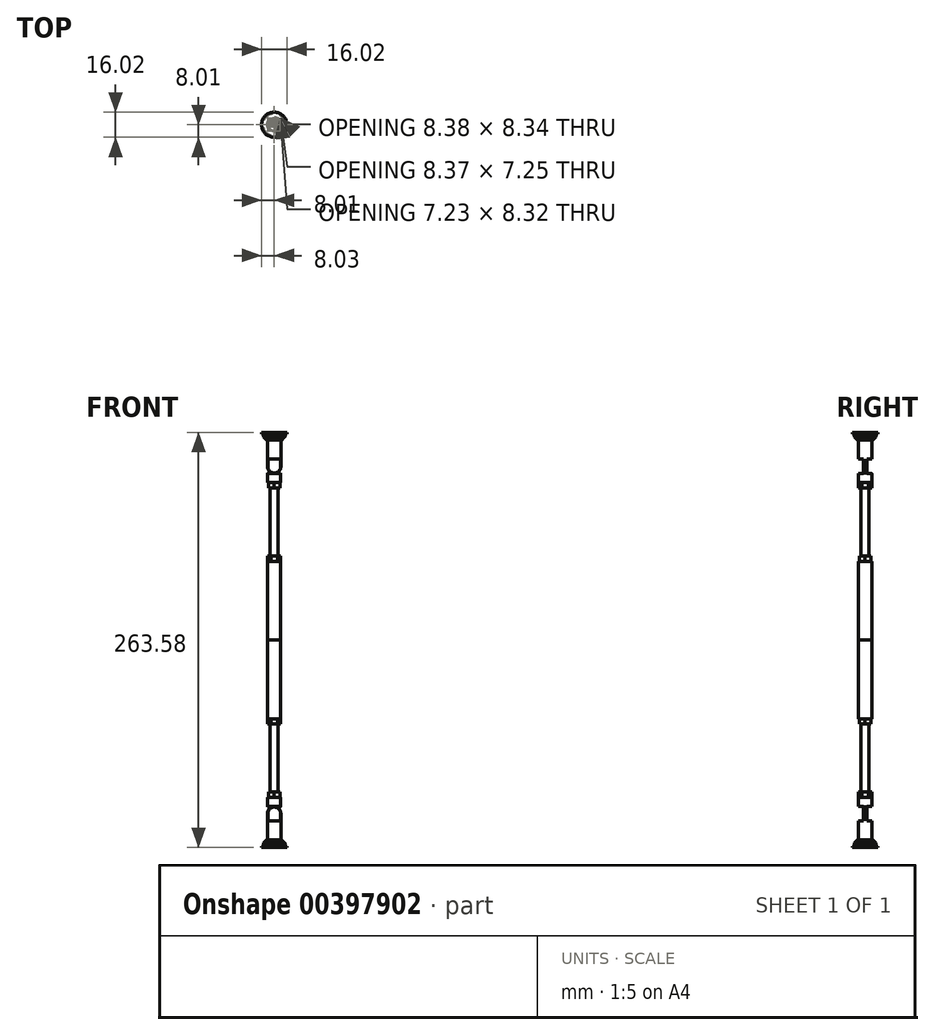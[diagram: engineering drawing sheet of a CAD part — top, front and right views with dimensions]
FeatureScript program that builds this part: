
annotation { "Feature Type Name" : "Feature", "Feature Type Description" : "" }
export const myFeature = defineFeature(function(context is Context, id is Id, definition is map)
    precondition{}
    {
        {
            var Q0;
            Q0=qCreatedBy(makeId("Top.planeOp"),FACE);
            var sketch = newSketch(context, id + "F0", { "sketchPlane" : qUnion([Q0])});
            skCircle(sketch, "E0", {"center": v(0, 0) * mm, "radius": 4.2 * mm});
            skSolve(sketch);
        }
        {
            var Q0;
            Q0 = qSketchRegion(id + "F0", true);
            extrude(context, id + "F1", {"entities" : qUnion([Q0]), "depth" : 50 * mm});
        }
        {
            var Q0;
            Q0=qCreatedBy(makeId("Top.planeOp"),FACE);
            var sketch = newSketch(context, id + "F2", { "sketchPlane" : qUnion([Q0])});
            skCircle(sketch, "E1", {"center": v(0, 0) * mm, "radius": 2.52 * mm});
            skSolve(sketch);
        }
        {
            var Q0;
            Q0 = qSketchRegion(id + "F2", true);
            extrude(context, id + "F3", {"entities" : qUnion([Q0]), "depth" : 100 * mm});
        }
        {
            var Q0;
            Q0=makeQuery(id+"F1.opExtrude","CAP_FACE",FACE,{"disambiguationData":[OSD([sQuery(id+"F0.wireOp",EDGE,"E0")])],"isStart":false});
            var sketch = newSketch(context, id + "F4", { "sketchPlane" : qUnion([Q0])});
            skCircle(sketch, "E2.cCircle", {"center": v(0, 0) * mm, "radius": 3.62 * mm, "construction": true});
            skLineSegment(sketch, "E2.0", {"start": v(-2.1, 3.62) * mm, "end": v(2.1, 3.62) * mm});
            skLineSegment(sketch, "E2.1", {"start": v(2.1, 3.62) * mm, "end": v(4.18, 0) * mm});
            skLineSegment(sketch, "E2.2", {"start": v(4.18, 0) * mm, "end": v(2.1, -3.62) * mm});
            skLineSegment(sketch, "E2.3", {"start": v(2.1, -3.62) * mm, "end": v(-2.1, -3.62) * mm});
            skLineSegment(sketch, "E2.4", {"start": v(-2.1, -3.62) * mm, "end": v(-4.18, 0) * mm});
            skLineSegment(sketch, "E2.5", {"start": v(-4.18, 0) * mm, "end": v(-2.1, 3.62) * mm});
            skPoint(sketch, "E2.0.midPoint", {"position": v(0, 3.62) * mm});
            skSolve(sketch);
        }
        {
            var Q0;
            Q0 = qSketchRegion(id + "F4", true);
            extrude(context, id + "F5", {"entities" : qUnion([Q0]), "operationType" : NewBodyOperationType.ADD, "depth" : 3.4 * mm});
        }
        {
            var Q0;
            Q0=makeQuery(id+"F3.opExtrude","CAP_FACE",FACE,{"disambiguationData":[OSD([sQuery(id+"F2.wireOp",EDGE,"E1")])],"isStart":false});
            var sketch = newSketch(context, id + "F6", { "sketchPlane" : qUnion([Q0])});
            skCircle(sketch, "E3.cCircle", {"center": v(0, 0) * mm, "radius": 3.6 * mm, "construction": true});
            skLineSegment(sketch, "E3.0", {"start": v(-3.61, 2.07) * mm, "end": v(-0.02, 4.16) * mm});
            skLineSegment(sketch, "E3.1", {"start": v(-0.02, 4.16) * mm, "end": v(3.6, 2.1) * mm});
            skLineSegment(sketch, "E3.2", {"start": v(3.6, 2.1) * mm, "end": v(3.61, -2.07) * mm});
            skLineSegment(sketch, "E3.3", {"start": v(3.61, -2.07) * mm, "end": v(0.02, -4.16) * mm});
            skLineSegment(sketch, "E3.4", {"start": v(0.02, -4.16) * mm, "end": v(-3.6, -2.1) * mm});
            skLineSegment(sketch, "E3.5", {"start": v(-3.6, -2.1) * mm, "end": v(-3.61, 2.07) * mm});
            skPoint(sketch, "E3.0.midPoint", {"position": v(-1.82, 3.11) * mm});
            skSolve(sketch);
        }
        {
            var Q0;
            Q0 = qSketchRegion(id + "F6", true);
            extrude(context, id + "F7", {"entities" : qUnion([Q0]), "operationType" : NewBodyOperationType.ADD, "oppositeDirection" : true, "depth" : 3.4 * mm});
        }
        {
            var Q0;
            Q0=makeQuery(id+"F7.boolean.opBoolean","MERGE",FACE,{"derivedFrom":[makeQuery(id+"F3.opExtrude","CAP_FACE",FACE,{"disambiguationData":[OSD([sQuery(id+"F2.wireOp",EDGE,"E1")])],"isStart":false}),makeQuery(id+"F7.opExtrude","CAP_FACE",FACE,{"disambiguationData":[OSD([sQuery(id+"F6.wireOp",EDGE,"E3.0"),sQuery(id+"F6.wireOp",EDGE,"E3.1"),sQuery(id+"F6.wireOp",EDGE,"E3.2"),sQuery(id+"F6.wireOp",EDGE,"E3.3"),sQuery(id+"F6.wireOp",EDGE,"E3.4"),sQuery(id+"F6.wireOp",EDGE,"E3.5")])],"isStart":true})]});
            var sketch = newSketch(context, id + "F8", { "sketchPlane" : qUnion([Q0])});
            skCircle(sketch, "E4", {"center": v(0, 0) * mm, "radius": 4.2 * mm});
            skSolve(sketch);
        }
        {
            var Q0;
            Q0 = qSketchRegion(id + "F8", true);
            extrude(context, id + "F9", {"entities" : qUnion([Q0]), "operationType" : NewBodyOperationType.ADD, "depth" : 14 * mm});
        }
        {
            var Q0;
            Q0=makeQuery(id+"F9.opExtrude","CAP_EDGE",EDGE,{"disambiguationData":[OSD([sQuery(id+"F8.wireOp",EDGE,"E4")])],"isStart":false});
            fillet(context, id + "F10", {"entities" : qUnion([Q0]), "radius" : 4.1 * mm, "tangentPropagation" : true, "allowEdgeOverflow" : false});
        }
        {
            var Q0;
            Q0=qCreatedBy(makeId("Right.planeOp"),FACE);
            var sketch = newSketch(context, id + "F11", { "sketchPlane" : qUnion([Q0])});
            skLineSegment(sketch, "E5", {"start": v(0, 159.45) * mm, "end": v(0, -678.37) * mm, "construction": true});
            skLineSegment(sketch, "E6.bottom", {"start": v(1.5, 116.74) * mm, "end": v(-1.5, 116.74) * mm});
            skLineSegment(sketch, "E6.top", {"start": v(1.5, 105.99) * mm, "end": v(-1.5, 105.99) * mm});
            skLineSegment(sketch, "E6.left", {"start": v(1.5, 116.74) * mm, "end": v(1.5, 105.99) * mm});
            skLineSegment(sketch, "E6.right", {"start": v(-1.5, 116.74) * mm, "end": v(-1.5, 105.99) * mm});
            skPoint(sketch, "E6.middle", {"position": v(0, 111.36) * mm});
            skSolve(sketch);
        }
        {
            var Q0;
            Q0 = qSketchRegion(id + "F11", true);
            extrude(context, id + "F12", {"entities" : qUnion([Q0]), "operationType" : NewBodyOperationType.REMOVE, "endBound" : BoundingType.SYMMETRIC, "oppositeDirection" : true, "depth" : 25 * mm});
        }
        {
            var Q0;
            Q0=makeQuery(id+"F12.boolean.opBoolean","COPY",FACE,{"derivedFrom":makeQuery(id+"F12.opExtrude","SWEPT_FACE",FACE,{"disambiguationData":[OSD([sQuery(id+"F11.wireOp",EDGE,"E6.left")])]})});
            var sketch = newSketch(context, id + "F13", { "sketchPlane" : qUnion([Q0])});
            skCircle(sketch, "E7", {"center": v(0, 109.9) * mm, "radius": 1.72 * mm});
            skSolve(sketch);
        }
        {
            var Q0;
            Q0 = qSketchRegion(id + "F13", true);
            extrude(context, id + "F14", {"entities" : qUnion([Q0]), "oppositeDirection" : true, "depth" : 3.5 * mm});
        }
        {
            var Q0;
            Q0=makeQuery(id+"F14.opExtrude","SWEPT_BODY",BODY,{"disambiguationData":[OSD([sQuery(id+"F13.wireOp",EDGE,"E7")])]});
            var Q1;
            Q1=qCreatedBy(makeId("Front.planeOp"),FACE);
            mirror(context, id + "F15", {"operationType" : NewBodyOperationType.ADD, "entities" : qUnion([Q0]), "mirrorPlane" : qUnion([Q1])});
        }
        {
            var Q0;
            Q0=makeQuery(id+"F12.boolean.opBoolean","COPY",FACE,{"derivedFrom":makeQuery(id+"F12.opExtrude","SWEPT_FACE",FACE,{"disambiguationData":[OSD([sQuery(id+"F11.wireOp",EDGE,"E6.top")])]})});
            var sketch = newSketch(context, id + "F16", { "sketchPlane" : qUnion([Q0])});
            skCircle(sketch, "E8", {"center": v(0, 0) * mm, "radius": 4.21 * mm});
            skSolve(sketch);
        }
        {
            var Q0;
            Q0 = qSketchRegion(id + "F16", true);
            extrude(context, id + "F17", {"entities" : qUnion([Q0]), "depth" : 25 * mm});
        }
        {
            var Q0;
            Q0=qCreatedBy(makeId("Right.planeOp"),FACE);
            var sketch = newSketch(context, id + "F18", { "sketchPlane" : qUnion([Q0])});
            skLineSegment(sketch, "E9.bottom", {"start": v(-1.2, 114.83) * mm, "end": v(-10.62, 114.83) * mm});
            skLineSegment(sketch, "E9.top", {"start": v(-1.2, 105.8) * mm, "end": v(-10.62, 105.8) * mm});
            skLineSegment(sketch, "E9.left", {"start": v(-1.2, 114.83) * mm, "end": v(-1.2, 105.8) * mm});
            skLineSegment(sketch, "E9.right", {"start": v(-10.62, 114.83) * mm, "end": v(-10.62, 105.8) * mm});
            skLineSegment(sketch, "E10.MirrorCS", {"start": v(1.2, 114.83) * mm, "end": v(1.2, 105.8) * mm});
            skLineSegment(sketch, "E11.MirrorCS", {"start": v(1.2, 114.83) * mm, "end": v(10.62, 114.83) * mm});
            skLineSegment(sketch, "E12.MirrorCS", {"start": v(10.62, 114.83) * mm, "end": v(10.62, 105.8) * mm});
            skLineSegment(sketch, "E13.MirrorCS", {"start": v(1.2, 105.8) * mm, "end": v(10.62, 105.8) * mm});
            skSolve(sketch);
        }
        {
            var Q0;
            Q0=makeQuery(id+"F17.opExtrude","CAP_EDGE",EDGE,{"disambiguationData":[OSD([sQuery(id+"F16.wireOp",EDGE,"E8")])],"isStart":true});
            fillet(context, id + "F19", {"entities" : qUnion([Q0]), "radius" : 4 * mm, "tangentPropagation" : true, "allowEdgeOverflow" : false});
        }
        {
            var Q0;
            Q0 = qSketchRegion(id + "F18", true);
            extrude(context, id + "F20", {"entities" : qUnion([Q0]), "operationType" : NewBodyOperationType.REMOVE, "endBound" : BoundingType.SYMMETRIC, "oppositeDirection" : true, "depth" : 25 * mm});
        }
        {
            var Q0;
            Q0=makeQuery(id+"F17.opExtrude","CAP_FACE",FACE,{"disambiguationData":[OSD([sQuery(id+"F16.wireOp",EDGE,"E8")])],"isStart":false});
            var sketch = newSketch(context, id + "F21", { "sketchPlane" : qUnion([Q0])});
            skCircle(sketch, "E14", {"center": v(0, 0) * mm, "radius": 6.87 * mm});
            skSolve(sketch);
        }
        {
            var Q0;
            Q0 = qSketchRegion(id + "F21", true);
            extrude(context, id + "F22", {"entities" : qUnion([Q0]), "operationType" : NewBodyOperationType.ADD, "oppositeDirection" : true, "depth" : 4 * mm});
        }
        {
            var Q0;
            Q0=makeQuery(id+"F22.opExtrude","CAP_EDGE",EDGE,{"disambiguationData":[OSD([sQuery(id+"F21.wireOp",EDGE,"E14")])],"isStart":false});
            chamfer(context, id + "F23", {"entities" : qUnion([Q0]), "width" : 2 * mm, "tangentPropagation" : true});
        }
        {
            var Q0;
            Q0=makeQuery(id+"F22.boolean.opBoolean","MERGE",FACE,{"derivedFrom":[makeQuery(id+"F17.opExtrude","CAP_FACE",FACE,{"disambiguationData":[OSD([sQuery(id+"F16.wireOp",EDGE,"E8")])],"isStart":false}),makeQuery(id+"F22.opExtrude","CAP_FACE",FACE,{"disambiguationData":[OSD([sQuery(id+"F21.wireOp",EDGE,"E14")])],"isStart":true})]});
            var sketch = newSketch(context, id + "F24", { "sketchPlane" : qUnion([Q0])});
            skCircle(sketch, "E15", {"center": v(0, 0) * mm, "radius": 8.01 * mm});
            skSolve(sketch);
        }
        {
            var Q0;
            Q0 = qSketchRegion(id + "F24", true);
            extrude(context, id + "F25", {"entities" : qUnion([Q0]), "operationType" : NewBodyOperationType.ADD, "depth" : 0.8 * mm});
        }
        {
            var Q0;
            Q0=makeQuery(id+"F1.opExtrude","SWEPT_BODY",BODY,{"disambiguationData":[OSD([sQuery(id+"F0.wireOp",EDGE,"E0")])]});
            var Q1;
            Q1=makeQuery(id+"F17.opExtrude","SWEPT_BODY",BODY,{"disambiguationData":[OSD([sQuery(id+"F16.wireOp",EDGE,"E8")])]});
            var Q2;
            Q2=makeQuery(id+"F3.opExtrude","SWEPT_BODY",BODY,{"disambiguationData":[OSD([sQuery(id+"F2.wireOp",EDGE,"E1")])]});
            var Q3;
            Q3=qCreatedBy(makeId("Top.planeOp"),FACE);
            mirror(context, id + "F26", {"entities" : qUnion([Q0, Q1, Q2]), "mirrorPlane" : qUnion([Q3])});
        }
    });
